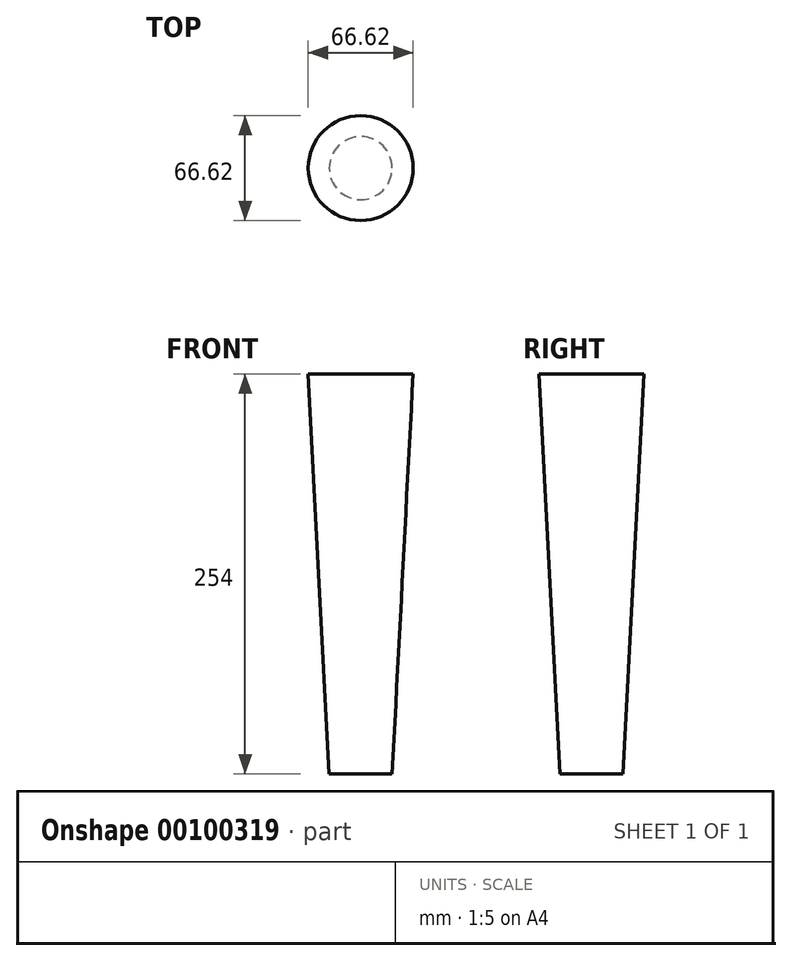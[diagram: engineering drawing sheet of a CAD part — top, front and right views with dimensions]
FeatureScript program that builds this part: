
annotation { "Feature Type Name" : "Feature", "Feature Type Description" : "" }
export const myFeature = defineFeature(function(context is Context, id is Id, definition is map)
    precondition{}
    {
        {
            var Q0;
            Q0=qCreatedBy(makeId("Top.planeOp"),FACE);
            var sketch = newSketch(context, id + "F0", { "sketchPlane" : qUnion([Q0])});
            skCircle(sketch, "E0", {"center": v(0, 0) * mm, "radius": 20 * mm});
            skSolve(sketch);
        }
        {
            var Q0;
            Q0 = qSketchRegion(id + "F0", true);
            extrude(context, id + "F1", {"entities" : qUnion([Q0]), "depth" : 254 * mm, "hasDraft" : true, "draftAngle" : 3 * degree});
        }
    });
